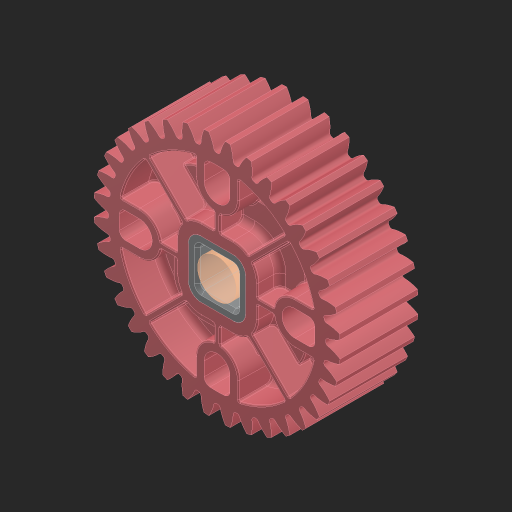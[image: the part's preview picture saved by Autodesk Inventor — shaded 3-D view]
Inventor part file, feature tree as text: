
AUTODESK INVENTOR PART (.ipt)
format: ipt  version: 2023 (Build 270158000, 158)  size: 2,128,384 bytes
history: native  units: in
note: dims shown in document units (in); Inventor stores cm internally (conversion verified against a paired STEP export)
features: other x3, sketch x1, extrude x1
ambient origin geometry x8: Origin, YZ Plane, XZ Plane, XY Plane, X Axis, Y Axis, Z Axis, Center Point
bodies: Solid1 (feature_tree), Solid2 (feature_tree)
feature tree (5):
  sketch  "Sketch1"  dims[d0=0.25in d1=0.3937in d2=0.0in]
  other  "Srf1"
  other  "276-7747-001_OVERMOLD Rev3_36T 24DP Gear Rev1_1:1"
  other  "276-7573-002 Rev7_2:1"
  extrude  "ExtrusionSrf1"  Depth=0.3937in TaperAngle=0.0deg
